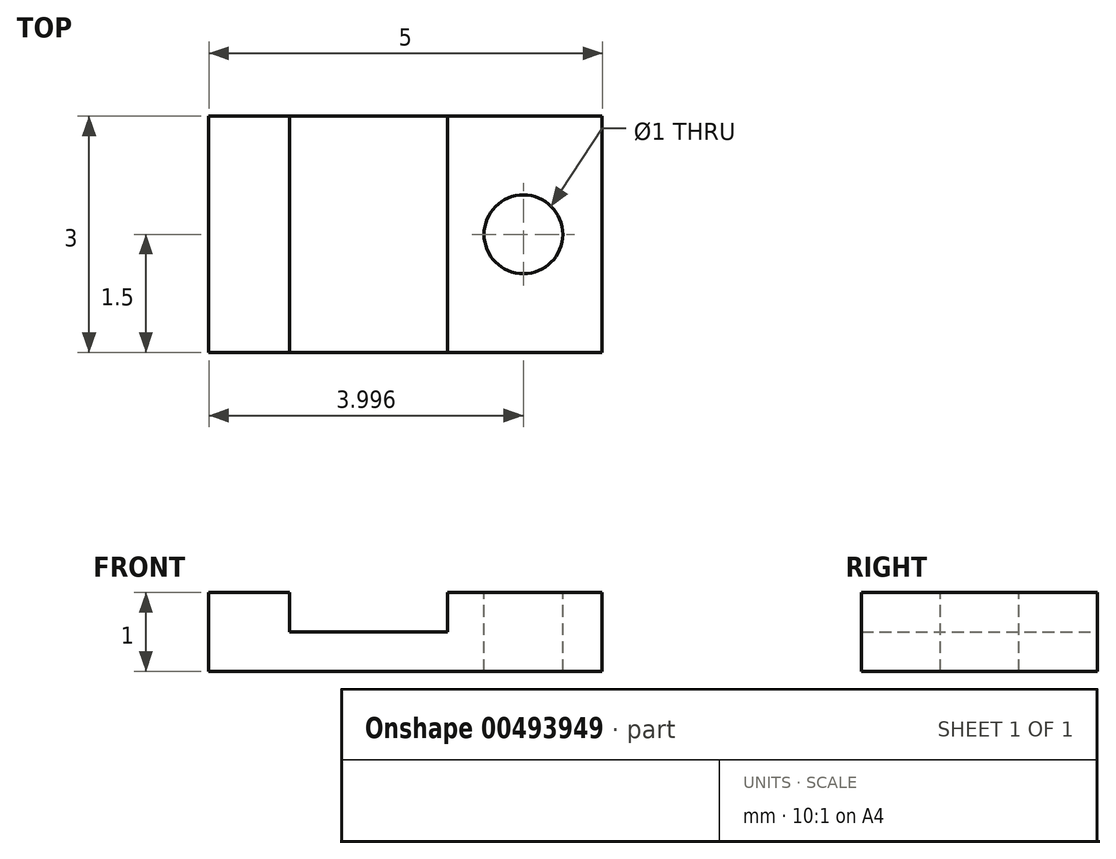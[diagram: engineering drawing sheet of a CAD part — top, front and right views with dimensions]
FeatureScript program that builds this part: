
annotation { "Feature Type Name" : "Feature", "Feature Type Description" : "" }
export const myFeature = defineFeature(function(context is Context, id is Id, definition is map)
    precondition{}
    {
        {
            var Q0;
            Q0=qCreatedBy(makeId("Front.planeOp"),FACE);
            var sketch = newSketch(context, id + "F0", { "sketchPlane" : qUnion([Q0])});
            skLineSegment(sketch, "E0.bottom", {"start": v(-2.1, 1) * mm, "end": v(2.9, 1) * mm});
            skLineSegment(sketch, "E0.top", {"start": v(-2.1, 0) * mm, "end": v(2.9, 0) * mm});
            skLineSegment(sketch, "E0.left", {"start": v(-2.1, 1) * mm, "end": v(-2.1, 0) * mm});
            skLineSegment(sketch, "E0.right", {"start": v(2.9, 1) * mm, "end": v(2.9, 0) * mm});
            skLineSegment(sketch, "E1.bottom", {"start": v(-1.06, 1) * mm, "end": v(0.94, 1) * mm});
            skLineSegment(sketch, "E1.top", {"start": v(-1.06, 0.5) * mm, "end": v(0.94, 0.5) * mm});
            skLineSegment(sketch, "E1.left", {"start": v(-1.06, 1) * mm, "end": v(-1.06, 0.5) * mm});
            skLineSegment(sketch, "E1.right", {"start": v(0.94, 1) * mm, "end": v(0.94, 0.5) * mm});
            skSolve(sketch);
        }
        {
            var Q0;
            Q0=makeQuery(id+"F0.imprint","IMPRINT",FACE,{"disambiguationData":[TD([[makeQuery(id+"F0.imprint","IMPRINT",EDGE,{"derivedFrom":sQuery(id+"F0.wireOp",EDGE,"E0.top")}),1.0]])]});
            extrude(context, id + "F1", {"entities" : qUnion([Q0]), "depth" : 3 * mm});
        }
        {
            var Q0;
            {var subQ0=sQuery(id+"F0.wireOp",EDGE,"E0.bottom");Q0=makeQuery(id+"F1.opExtrude","SWEPT_FACE",FACE,{"disambiguationData":[OSD([subQ0]),TDD([makeQuery(id+"F0.imprint","IMPRINT",EDGE,{"disambiguationData":[TD([[makeQuery(id+"F0.imprint","INTERSECT",VERTEX,{"derivedFrom":[subQ0,sQuery(id+"F0.wireOp",EDGE,"E0.right")]}),1.0]])],"derivedFrom":subQ0})])]});}
            var sketch = newSketch(context, id + "F2", { "sketchPlane" : qUnion([Q0])});
            skCircle(sketch, "E2", {"center": v(1.9, -1.5) * mm, "radius": 0.5 * mm});
            skSolve(sketch);
        }
        {
            var Q0;
            Q0 = qSketchRegion(id + "F2", true);
            extrude(context, id + "F3", {"entities" : qUnion([Q0]), "operationType" : NewBodyOperationType.REMOVE, "oppositeDirection" : true, "depth" : 25 * mm});
        }
    });
